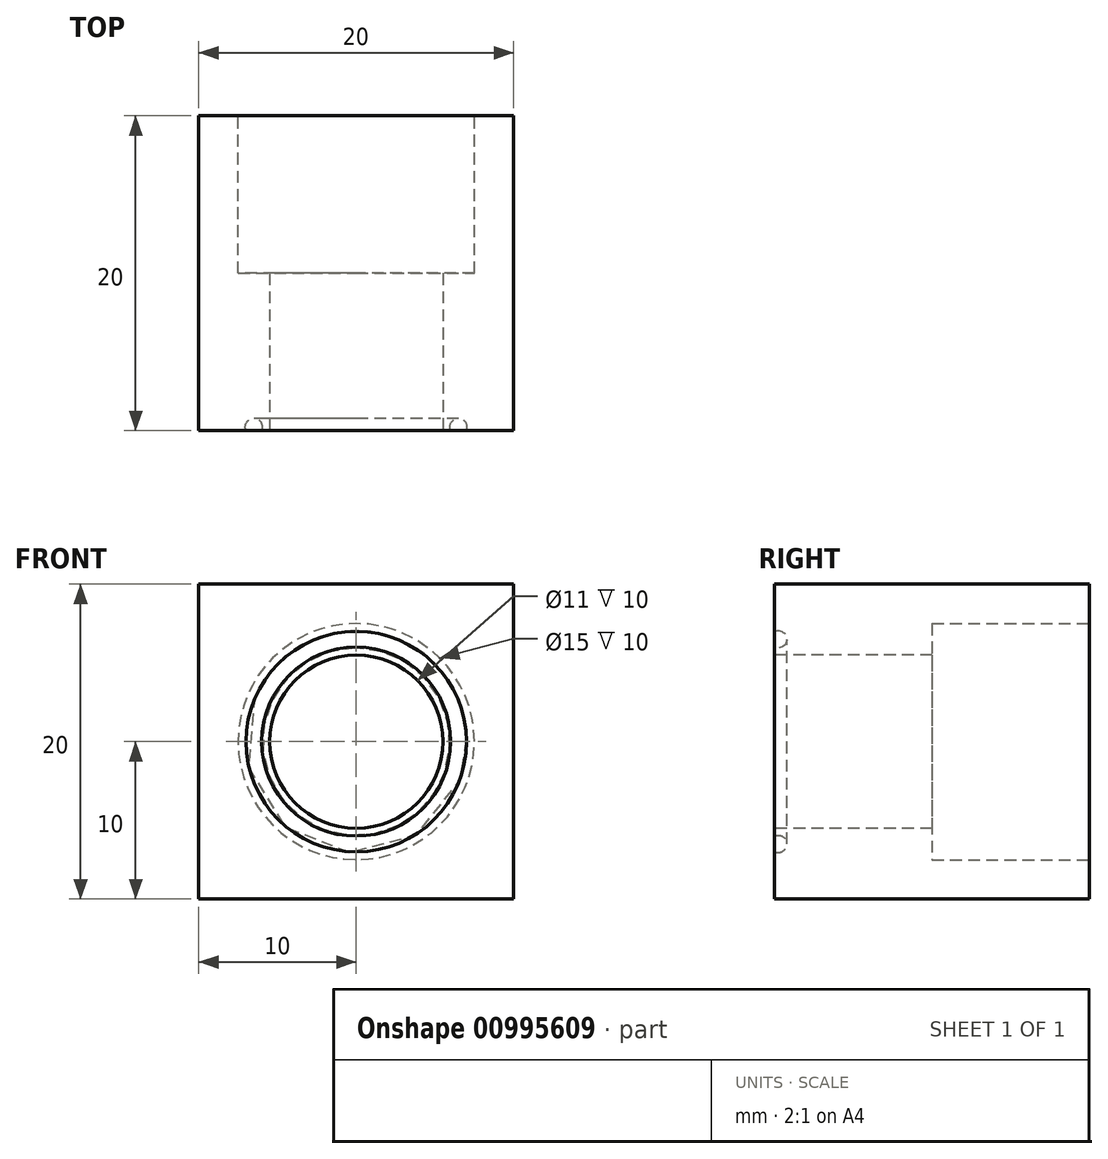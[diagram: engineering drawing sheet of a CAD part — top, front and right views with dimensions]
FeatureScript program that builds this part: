
annotation { "Feature Type Name" : "Feature", "Feature Type Description" : "" }
export const myFeature = defineFeature(function(context is Context, id is Id, definition is map)
    precondition{}
    {
        {
            var Q0;
            Q0=qCreatedBy(makeId("Front.planeOp"),FACE);
            var sketch = newSketch(context, id + "F0", { "sketchPlane" : qUnion([Q0])});
            skLineSegment(sketch, "E0.bottom", {"start": v(0, 0) * mm, "end": v(-20, 0) * mm});
            skLineSegment(sketch, "E0.top", {"start": v(0, 20) * mm, "end": v(-20, 20) * mm});
            skLineSegment(sketch, "E0.left", {"start": v(0, 0) * mm, "end": v(0, 20) * mm});
            skLineSegment(sketch, "E0.right", {"start": v(-20, 0) * mm, "end": v(-20, 20) * mm});
            skCircle(sketch, "E1", {"center": v(-10, 10) * mm, "radius": 5.5 * mm});
            skSolve(sketch);
        }
        {
            var Q0;
            Q0 = qSketchRegion(id + "F0", true);
            extrude(context, id + "F1", {"entities" : qUnion([Q0]), "oppositeDirection" : true, "depth" : 20 * mm, "offsetDistance" : 25 * mm});
        }
        {
            var Q0;
            Q0=makeQuery(id+"F1.opExtrude","SWEPT_FACE",FACE,{"disambiguationData":[OSD([sQuery(id+"F0.wireOp",EDGE,"E0.left")])]});
            cPlane(context, id + "F2", {"entities" : qUnion([Q0]), "cplaneType" : CPlaneType.OFFSET, "offset" : 10 * mm, "oppositeDirection" : true, "width" : 150 * mm, "height" : 150 * mm});
        }
        {
            var Q0;
            Q0=qCreatedBy(id+"F2.planeOp",FACE);
            var sketch = newSketch(context, id + "F3", { "sketchPlane" : qUnion([Q0])});
            skLineSegment(sketch, "E2", {"start": v(0, 17) * mm, "end": v(0, 16) * mm});
            skArc(sketch, "E3", {"start": v(0, 16) * mm, "mid": v(0.78, 16.5) * mm, "end": v(0, 17) * mm});
            skPoint(sketch, "E4", {"position": v(0, 16.5) * mm});
            skLineSegment(sketch, "E5", {"start": v(0, 10) * mm, "end": v(13, 10) * mm, "construction": true});
            skSolve(sketch);
        }
        {
            var Q0;
            Q0 = qSketchRegion(id + "F3", true);
            var Q1;
            Q1=sQuery(id+"F3.wireOp",EDGE,"E5");
            revolve(context, id + "F4", {"operationType" : NewBodyOperationType.REMOVE, "surfaceOperationType" : NewSurfaceOperationType.NEW, "entities" : qUnion([Q0]), "axis" : qUnion([Q1]), "revolveType" : RevolveType.FULL, "oppositeDirection" : true});
        }
        {
            var Q0;
            Q0=makeQuery(id+"F1.opExtrude","CAP_FACE",FACE,{"disambiguationData":[OSD([sQuery(id+"F0.wireOp",EDGE,"E0.bottom"),sQuery(id+"F0.wireOp",EDGE,"E0.top"),sQuery(id+"F0.wireOp",EDGE,"E0.left"),sQuery(id+"F0.wireOp",EDGE,"E0.right"),sQuery(id+"F0.wireOp",EDGE,"E1")])],"isStart":false});
            var sketch = newSketch(context, id + "F5", { "sketchPlane" : qUnion([Q0])});
            skCircle(sketch, "E6", {"center": v(10, 10) * mm, "radius": 7.5 * mm});
            skSolve(sketch);
        }
        {
            var Q0;
            Q0 = qSketchRegion(id + "F5", true);
            extrude(context, id + "F6", {"entities" : qUnion([Q0]), "operationType" : NewBodyOperationType.REMOVE, "oppositeDirection" : true, "depth" : 10 * mm, "offsetDistance" : 25 * mm});
        }
    });
